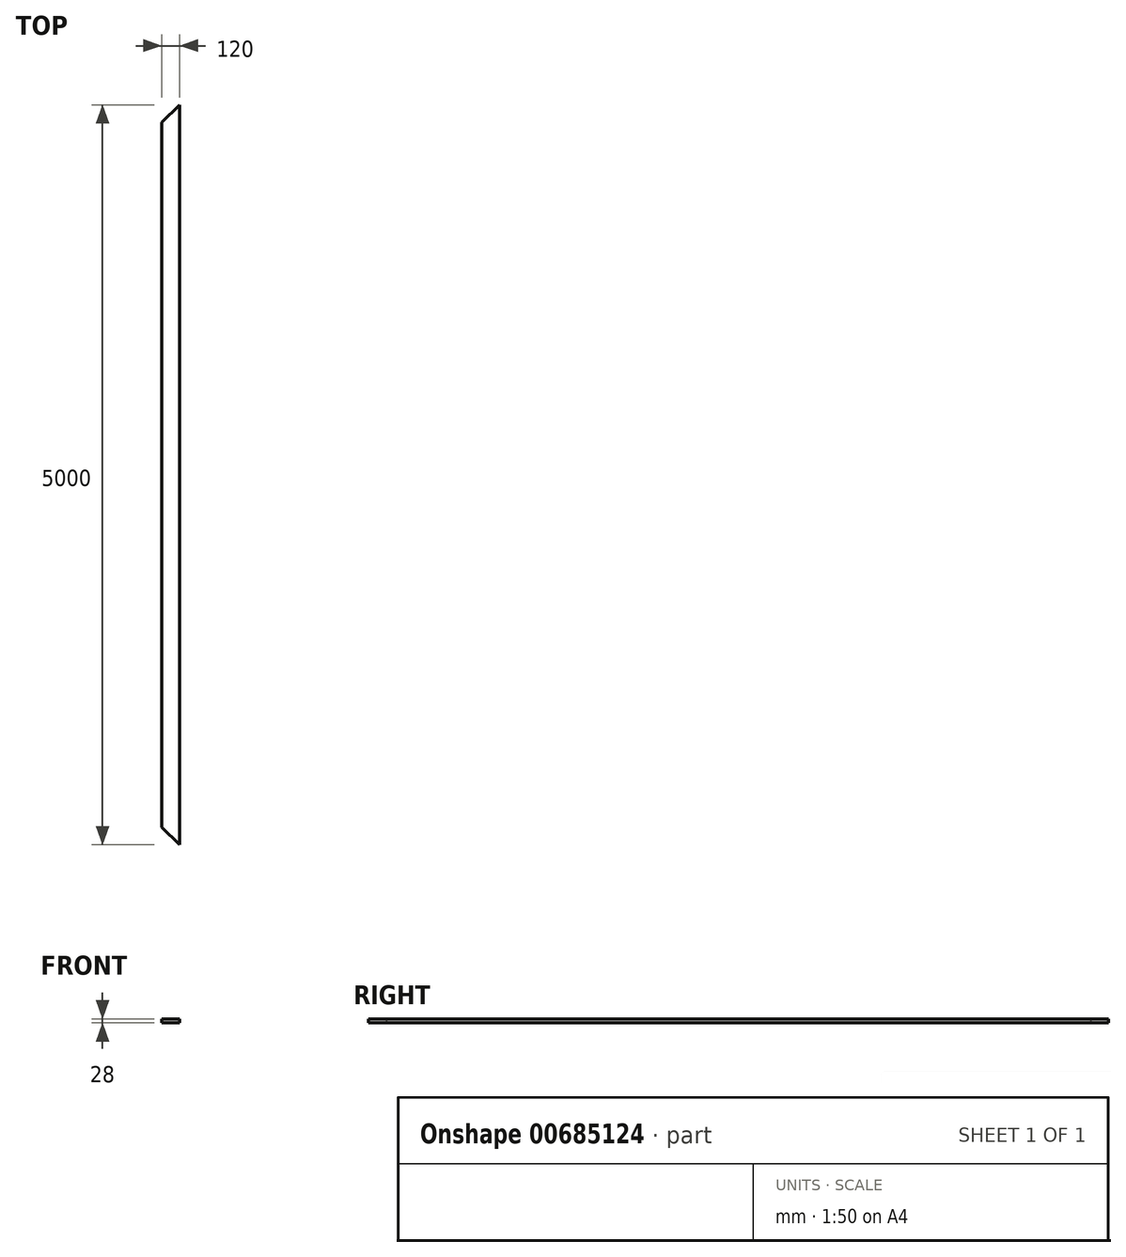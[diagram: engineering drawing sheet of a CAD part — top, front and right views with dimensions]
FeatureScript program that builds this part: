
annotation { "Feature Type Name" : "Feature", "Feature Type Description" : "" }
export const myFeature = defineFeature(function(context is Context, id is Id, definition is map)
    precondition{}
    {
        {
            var Q0;
            Q0=qCreatedBy(makeId("Top.planeOp"),FACE);
            var sketch = newSketch(context, id + "F0", { "sketchPlane" : qUnion([Q0])});
            skLineSegment(sketch, "E0", {"start": v(41.39, -935.05) * mm, "end": v(41.39, 4064.95) * mm});
            skLineSegment(sketch, "E1", {"start": v(41.39, 4064.95) * mm, "end": v(-78.61, 3944.95) * mm});
            skLineSegment(sketch, "E2", {"start": v(-78.61, 3944.95) * mm, "end": v(-78.61, -815.05) * mm});
            skLineSegment(sketch, "E3", {"start": v(-78.61, -815.05) * mm, "end": v(41.39, -935.05) * mm});
            skSolve(sketch);
        }
        {
            var Q0;
            Q0=qSketchRegion(id+"F0",true);
            extrude(context, id + "F1", {"entities" : qUnion([Q0]), "depth" : 28 * mm, "offsetDistance" : 25 * mm});
        }
    });
